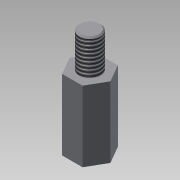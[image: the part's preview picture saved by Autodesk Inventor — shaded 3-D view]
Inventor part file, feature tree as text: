
AUTODESK INVENTOR PART (.ipt)
format: ipt  version: 2014 (Build 180170000, 170)  size: 124,928 bytes
history: native  units: mm
features: sketch x3, extrude x2, chamfer x2, hole x1, plane x1, mirror x1
ambient origin geometry x8: Origin, YZ Plane, XZ Plane, XY Plane, X Axis, Y Axis, Z Axis, Center Point
bodies: Solid1 (feature_tree)
feature tree (10):
  extrude  "Extrusion1"  Depth=10.0mm TaperAngle=0.0deg
  hole  "Hole1"  [1 undecoded]
  chamfer  "Chamfer2"  Distance=1.0mm
  extrude  "Extrusion3"  [1 undecoded]
  plane  "Work Plane1"
  mirror  "Mirror2"
  chamfer  "Chamfer3"  [1 undecoded]
  sketch  "Sketch1"  dims[d0=5.0mm d1=10.0mm d2=0.0mm]
  sketch  "Sketch3"  dims[d11=2.459mm d12=10.0mm d13=4.0mm d14=2.0mm d15=90.0deg d16=8.0mm d17=20.594885mm d18=0.5mm d19=2.0mm d20=45.0deg d21=1.0mm d22=-7.853982mm]
  sketch  "Sketch4"  dims[d23=0.5mm d24=2.0mm d25=45.0deg]
note: 3 required parameter values undecoded (feature->parameter linkage not recoverable at this tier; creation-order binding heuristic only, values carry confidence <= 0.55)
